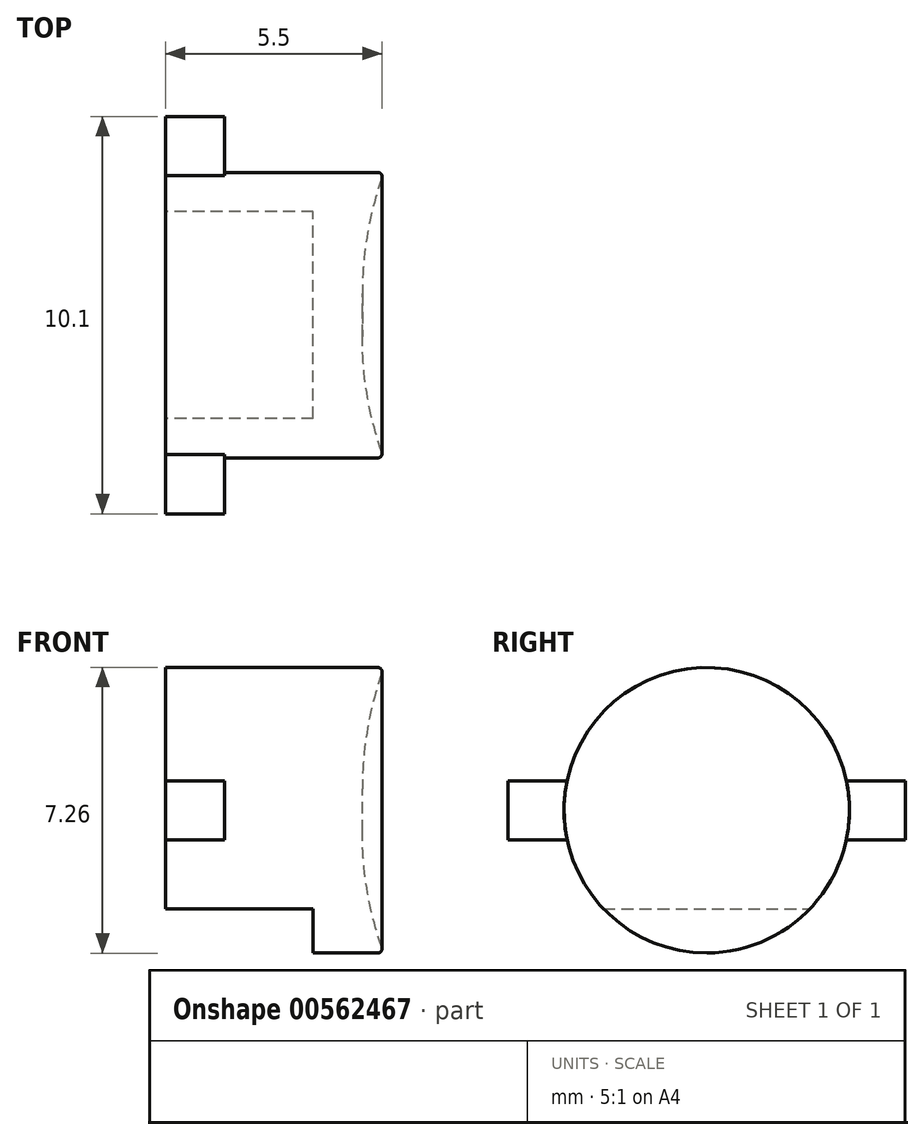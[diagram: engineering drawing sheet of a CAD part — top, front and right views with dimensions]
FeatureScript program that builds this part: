
annotation { "Feature Type Name" : "Feature", "Feature Type Description" : "" }
export const myFeature = defineFeature(function(context is Context, id is Id, definition is map)
    precondition{}
    {
        {
            var Q0;
            Q0=qCreatedBy(makeId("Right.planeOp"),FACE);
            var sketch = newSketch(context, id + "F0", { "sketchPlane" : qUnion([Q0])});
            skCircle(sketch, "E0", {"center": v(0, 0) * mm, "radius": 3.62 * mm});
            skSolve(sketch);
        }
        {
            var Q0;
            Q0=makeQuery(id+"F0.imprint","IMPRINT",FACE,{"disambiguationData":[TD([[makeQuery(id+"F0.imprint","IMPRINT",EDGE,{"derivedFrom":sQuery(id+"F0.wireOp",EDGE,"E0")}),1.0]])]});
            extrude(context, id + "F1", {"entities" : qUnion([Q0]), "depth" : 5.5 * mm, "offsetDistance" : 25 * mm, "symmetric" : true});
        }
        {
            var Q0;
            Q0=makeQuery(id+"F1.opExtrude","CAP_FACE",FACE,{"disambiguationData":[OSD([sQuery(id+"F0.wireOp",EDGE,"E0")])],"isStart":true});
            var sketch = newSketch(context, id + "F2", { "sketchPlane" : qUnion([Q0])});
            skLineSegment(sketch, "E1.left", {"start": v(5.05, -0.75) * mm, "end": v(5.05, 0.75) * mm});
            skLineSegment(sketch, "E2.left", {"start": v(-5.05, 0.75) * mm, "end": v(-5.05, -0.75) * mm});
            skLineSegment(sketch, "E3", {"start": v(5.05, 0.75) * mm, "end": v(3.55, 0.75) * mm});
            skLineSegment(sketch, "E4", {"start": v(5.05, -0.75) * mm, "end": v(3.55, -0.75) * mm});
            skArc(sketch, "E5", {"start": v(-3.55, 0.75) * mm, "mid": v(-3.63, 0) * mm, "end": v(-3.55, -0.75) * mm});
            skLineSegment(sketch, "E6", {"start": v(-5.05, 0.75) * mm, "end": v(-3.55, 0.75) * mm});
            skLineSegment(sketch, "E7", {"start": v(-5.05, -0.75) * mm, "end": v(-3.55, -0.75) * mm});
            skArc(sketch, "E8.trimOffspring", {"start": v(3.55, -0.75) * mm, "mid": v(3.63, 0) * mm, "end": v(3.55, 0.75) * mm});
            skPoint(sketch, "E9", {"position": v(5.05, 0) * mm});
            skPoint(sketch, "E10", {"position": v(-5.05, 0) * mm});
            skSolve(sketch);
        }
        {
            var Q0;
            Q0=qSketchRegion(id+"F2",true);
            extrude(context, id + "F3", {"entities" : qUnion([Q0]), "operationType" : NewBodyOperationType.ADD, "oppositeDirection" : true, "depth" : 1.5 * mm, "offsetDistance" : 25 * mm});
        }
        {
            var Q0;
            Q0=makeQuery(id+"F1.opExtrude","CAP_FACE",FACE,{"disambiguationData":[OSD([sQuery(id+"F0.wireOp",EDGE,"E0")])],"isStart":false});
            var sketch = newSketch(context, id + "F4", { "sketchPlane" : qUnion([Q0])});
            skCircle(sketch, "E11", {"center": v(0, 0) * mm, "radius": 3.5 * mm});
            skSolve(sketch);
        }
        {
            var Q0;
            Q0=qSketchRegion(id+"F4",true);
            extrude(context, id + "F5", {"entities" : qUnion([Q0]), "operationType" : NewBodyOperationType.REMOVE, "oppositeDirection" : true, "depth" : .5 * mm, "offsetDistance" : 25 * mm});
        }
        {
            var Q0;
            Q0=makeQuery(id+"F3.boolean.opBoolean","MERGE",FACE,{"derivedFrom":[makeQuery(id+"F1.opExtrude","CAP_FACE",FACE,{"disambiguationData":[OSD([sQuery(id+"F0.wireOp",EDGE,"E0")])],"isStart":true}),makeQuery(id+"F3.opExtrude","CAP_FACE",FACE,{"disambiguationData":[OSD([sQuery(id+"F2.wireOp",EDGE,"E1.left"),sQuery(id+"F2.wireOp",EDGE,"E3"),sQuery(id+"F2.wireOp",EDGE,"E4"),sQuery(id+"F2.wireOp",EDGE,"E8.trimOffspring")])],"isStart":true}),makeQuery(id+"F3.opExtrude","CAP_FACE",FACE,{"disambiguationData":[OSD([sQuery(id+"F2.wireOp",EDGE,"E2.left"),sQuery(id+"F2.wireOp",EDGE,"E5"),sQuery(id+"F2.wireOp",EDGE,"E6"),sQuery(id+"F2.wireOp",EDGE,"E7")])],"isStart":true})]});
            var sketch = newSketch(context, id + "F6", { "sketchPlane" : qUnion([Q0])});
            skArc(sketch, "E12", {"start": v(-2.62, -2.5) * mm, "mid": v(0, -3.63) * mm, "end": v(2.63, -2.5) * mm});
            skLineSegment(sketch, "E13", {"start": v(2.63, -2.5) * mm, "end": v(-2.62, -2.5) * mm});
            skSolve(sketch);
        }
        {
            var Q0;
            Q0=qSketchRegion(id+"F6",true);
            extrude(context, id + "F7", {"entities" : qUnion([Q0]), "operationType" : NewBodyOperationType.REMOVE, "oppositeDirection" : true, "depth" : 3.75 * mm, "offsetDistance" : 25 * mm});
        }
        {
            var Q0;
            Q0=makeQuery(id+"F5.boolean.opBoolean","COPY",FACE,{"derivedFrom":makeQuery(id+"F5.opExtrude","CAP_FACE",FACE,{"disambiguationData":[OSD([sQuery(id+"F4.wireOp",EDGE,"E11")])],"isStart":false})});
            fillet(context, id + "F8", {"entities" : qUnion([Q0]), "radius" : 9 * mm, "tangentPropagation" : true, "allowEdgeOverflow" : false});
        }
        {
            var Q0;
            Q0=makeQuery(id+"F8.opFillet","BLEND_EDGE",EDGE,{"blendedFrom":[makeQuery(id+"F5.boolean.opBoolean","COPY",EDGE,{"derivedFrom":makeQuery(id+"F5.opExtrude","CAP_EDGE",EDGE,{"disambiguationData":[OSD([sQuery(id+"F4.wireOp",EDGE,"E11")])],"isStart":false})}),makeQuery(id+"F1.opExtrude","CAP_FACE",FACE,{"disambiguationData":[OSD([sQuery(id+"F0.wireOp",EDGE,"E0")])],"isStart":false})],"blendedInto":[makeQuery(id+"F1.opExtrude","CAP_FACE",FACE,{"disambiguationData":[OSD([sQuery(id+"F0.wireOp",EDGE,"E0")])],"isStart":false})]});
            var Q1;
            Q1=makeQuery(id+"F1.opExtrude","CAP_EDGE",EDGE,{"disambiguationData":[OSD([sQuery(id+"F0.wireOp",EDGE,"E0")])],"isStart":false});
            fillet(context, id + "F9", {"entities" : qUnion([Q0, Q1]), "radius" : .1 * mm, "tangentPropagation" : true, "allowEdgeOverflow" : false});
        }
    });
